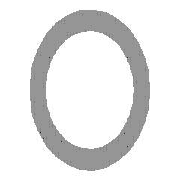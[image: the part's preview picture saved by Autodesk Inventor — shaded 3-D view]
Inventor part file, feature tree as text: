
AUTODESK INVENTOR PART (.ipt)
format: ipt  version: 2021 (Build 250183000, 183)  size: 378,880 bytes
history: native  units: mm (DEFAULTED — no unit token found)
features: other x7, plane x3, sketch x3, sweep x1, split x1
ambient origin geometry x8: Origin, YZ Plane, XZ Plane, XY Plane, X Axis, Y Axis, Z Axis, Center Point
bodies: Solid1 (feature_tree)
feature tree (15):
  parser-record x1  (decoder bookkeeping rows leaked as tree rows — omitted from the tree; the rows remain in map.json)
  other  "Driven Length"
  other  "Plano inicial"
  other  "Plano final"
  other  "Trayectoria de barrido"
  plane  "Plano de trabajo de orientación"
  sweep  "Cuerpo"
  plane  "Plano de trabajo10"
  split  "Dividir6"
  sketch  "Sketch3"  dims[d0=26.67mm d1=3.9116mm]
  plane  "Work Plane3"
  sketch  "Sketch4"  dims[d4=-0.0mm]
  sketch  "Boceto10"  dims[d5=1126.193571mm d6=90.0deg d7=1126.193571mm d8=0.0mm d9=0.0mm d30=0.0mm d31=90.0deg d32=0.0mm d33=90.0deg]
  other  "Sup6"
  other  "SuperficieSolevación6"
